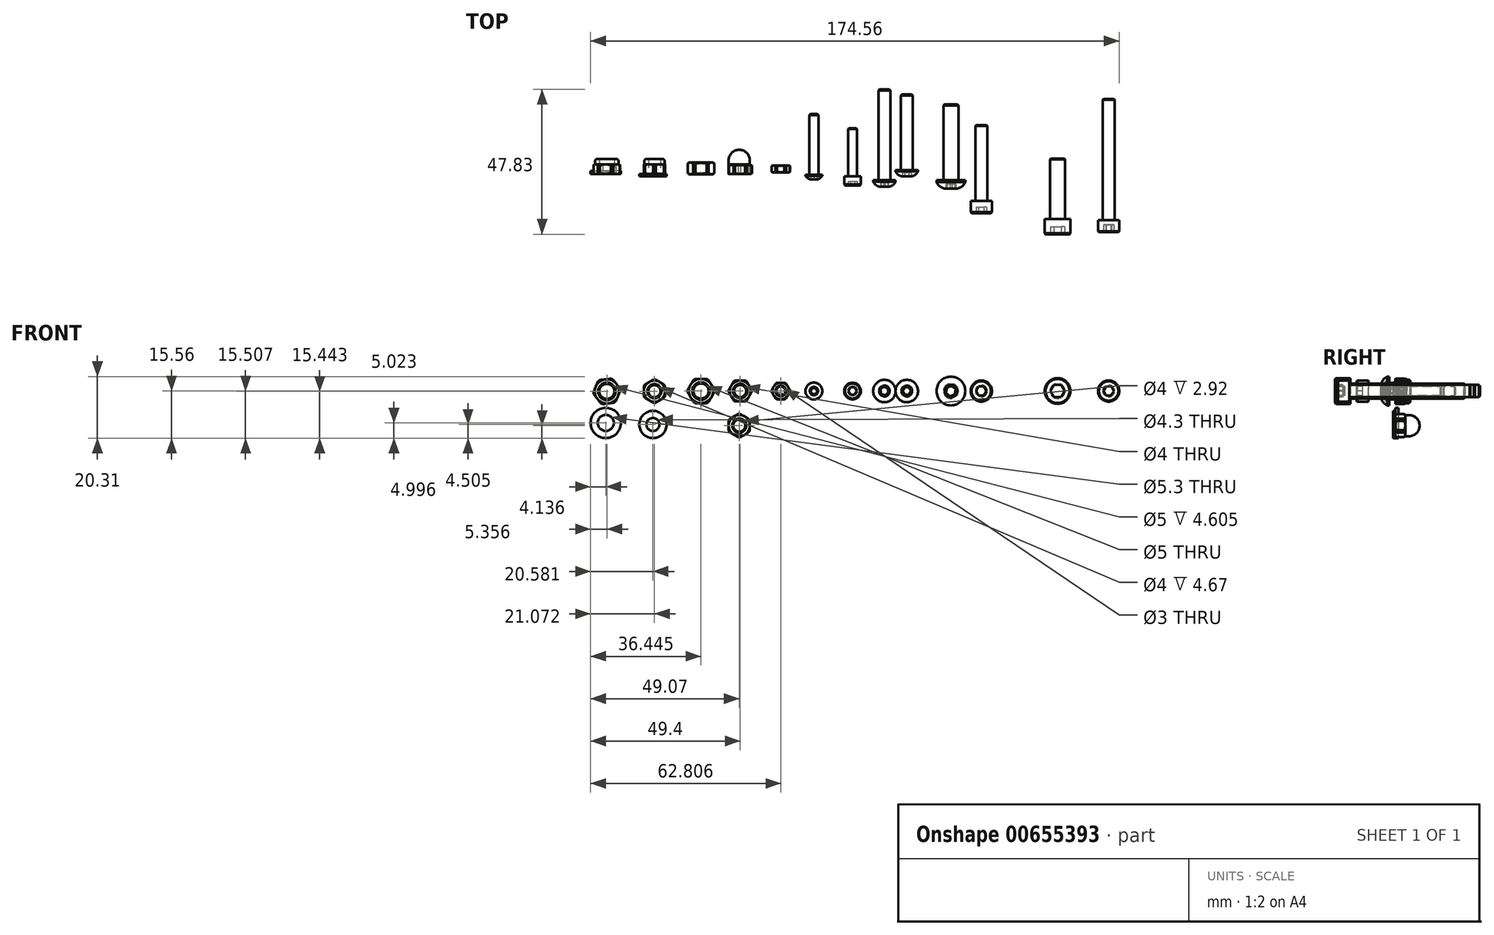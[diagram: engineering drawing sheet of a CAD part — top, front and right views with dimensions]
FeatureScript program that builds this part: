
annotation { "Feature Type Name" : "Feature", "Feature Type Description" : "" }
export const myFeature = defineFeature(function(context is Context, id is Id, definition is map)
    precondition{}
    {
        {
            var Q0;
            Q0=qCreatedBy(makeId("Top.planeOp"),FACE);
            var sketch = newSketch(context, id + "F0", { "sketchPlane" : qUnion([Q0])});
            skLineSegment(sketch, "E0.bottom", {"start": v(-2, 0) * mm, "end": v(-3.83, 0) * mm});
            skLineSegment(sketch, "E0.top", {"start": v(-2, 3) * mm, "end": v(-3.83, 3) * mm});
            skLineSegment(sketch, "E0.left", {"start": v(-2, 0) * mm, "end": v(-2, 3) * mm});
            skLineSegment(sketch, "E0.right", {"start": v(-3.83, 0) * mm, "end": v(-3.83, 3) * mm});
            skLineSegment(sketch, "E1", {"start": v(-2, 0) * mm, "end": v(0, 0) * mm, "construction": true});
            skLineSegment(sketch, "E2", {"start": v(0, 0) * mm, "end": v(0, 3) * mm, "construction": true});
            skSolve(sketch);
        }
        {
            var Q0;
            Q0 = qSketchRegion(id + "F0", true);
            var Q1;
            Q1=sQuery(id+"F0.wireOp",EDGE,"E2");
            revolve(context, id + "F1", {"entities" : qUnion([Q0]), "axis" : qUnion([Q1]), "revolveType" : RevolveType.FULL});
        }
        {
            var Q0;
            Q0=makeQuery(id+"F1.opRevolve","SWEPT_EDGE",EDGE,{"disambiguationData":[OSD([sQuery(id+"F0.wireOp",EDGE,"E0.bottom"),sQuery(id+"F0.wireOp",EDGE,"E0.right")])]});
            var Q1;
            Q1=makeQuery(id+"F1.opRevolve","SWEPT_EDGE",EDGE,{"disambiguationData":[OSD([sQuery(id+"F0.wireOp",EDGE,"E0.top"),sQuery(id+"F0.wireOp",EDGE,"E0.right")])]});
            var Q2;
            Q2=makeQuery(id+"F1.opRevolve","SWEPT_EDGE",EDGE,{"disambiguationData":[OSD([sQuery(id+"F0.wireOp",EDGE,"E0.bottom"),sQuery(id+"F0.wireOp",EDGE,"E0.left")])]});
            var Q3;
            Q3=makeQuery(id+"F1.opRevolve","SWEPT_EDGE",EDGE,{"disambiguationData":[OSD([sQuery(id+"F0.wireOp",EDGE,"E0.top"),sQuery(id+"F0.wireOp",EDGE,"E0.left")])]});
            chamfer(context, id + "F2", {"entities" : qUnion([Q0, Q1, Q2, Q3]), "chamferType" : ChamferType.OFFSET_ANGLE, "width" : 0.77 * mm / 2, "oppositeDirection" : false, "angle" : 30 * degree, "tangentPropagation" : true});
        }
        {
            var Q0;
            Q0=makeQuery(id+"F1.opRevolve","SWEPT_FACE",FACE,{"disambiguationData":[OSD([sQuery(id+"F0.wireOp",EDGE,"E0.bottom")])]});
            var sketch = newSketch(context, id + "F3", { "sketchPlane" : qUnion([Q0])});
            skCircle(sketch, "E3.cCircle", {"center": v(0, 0) * mm, "radius": 3.45 * mm, "construction": true});
            skLineSegment(sketch, "E3.0", {"start": v(3.98, 0) * mm, "end": v(2, -3.45) * mm});
            skLineSegment(sketch, "E3.1", {"start": v(2, -3.45) * mm, "end": v(-2, -3.45) * mm});
            skLineSegment(sketch, "E3.2", {"start": v(-2, -3.45) * mm, "end": v(-3.98, 0) * mm});
            skLineSegment(sketch, "E3.3", {"start": v(-3.98, 0) * mm, "end": v(-2, 3.45) * mm});
            skLineSegment(sketch, "E3.4", {"start": v(-2, 3.45) * mm, "end": v(2, 3.45) * mm});
            skLineSegment(sketch, "E3.5", {"start": v(2, 3.45) * mm, "end": v(3.98, 0) * mm});
            skPoint(sketch, "E3.0.midPoint", {"position": v(2.99, -1.73) * mm});
            skCircle(sketch, "E4", {"center": v(0, 0) * mm, "radius": 4.53 * mm});
            skSolve(sketch);
        }
        {
            var Q0;
            Q0 = qSketchRegion(id + "F3", true);
            extrude(context, id + "F4", {"entities" : qUnion([Q0]), "operationType" : NewBodyOperationType.REMOVE, "oppositeDirection" : true, "depth" : 25 * mm, "offsetDistance" : 25 * mm});
        }
        {
            var Q0;
            Q0=qCreatedBy(makeId("Top.planeOp"),FACE);
            var sketch = newSketch(context, id + "F5", { "sketchPlane" : qUnion([Q0])});
            skLineSegment(sketch, "E5.bottom", {"start": v(10.4, 2.85) * mm, "end": v(11.9, 2.85) * mm});
            skLineSegment(sketch, "E5.top", {"start": v(10.4, 0.58) * mm, "end": v(11.9, 0.58) * mm});
            skLineSegment(sketch, "E5.left", {"start": v(10.4, 2.85) * mm, "end": v(10.4, 0.58) * mm});
            skLineSegment(sketch, "E5.right", {"start": v(11.9, 2.85) * mm, "end": v(11.9, 0.58) * mm});
            skLineSegment(sketch, "E6", {"start": v(11.9, 0.58) * mm, "end": v(13.4, 0.58) * mm, "construction": true});
            skLineSegment(sketch, "E7", {"start": v(13.4, 0.58) * mm, "end": v(13.4, 2.85) * mm, "construction": true});
            skSolve(sketch);
        }
        {
            var Q0;
            Q0 = qSketchRegion(id + "F5", true);
            var Q1;
            Q1=sQuery(id+"F5.wireOp",EDGE,"E7");
            revolve(context, id + "F6", {"entities" : qUnion([Q0]), "axis" : qUnion([Q1]), "revolveType" : RevolveType.FULL});
        }
        {
            var Q0;
            Q0=makeQuery(id+"F6.opRevolve","SWEPT_EDGE",EDGE,{"disambiguationData":[OSD([sQuery(id+"F5.wireOp",EDGE,"E5.top"),sQuery(id+"F5.wireOp",EDGE,"E5.right")])]});
            var Q1;
            Q1=makeQuery(id+"F6.opRevolve","SWEPT_EDGE",EDGE,{"disambiguationData":[OSD([sQuery(id+"F5.wireOp",EDGE,"E5.top"),sQuery(id+"F5.wireOp",EDGE,"E5.left")])]});
            var Q2;
            Q2=makeQuery(id+"F6.opRevolve","SWEPT_EDGE",EDGE,{"disambiguationData":[OSD([sQuery(id+"F5.wireOp",EDGE,"E5.bottom"),sQuery(id+"F5.wireOp",EDGE,"E5.right")])]});
            var Q3;
            Q3=makeQuery(id+"F6.opRevolve","SWEPT_EDGE",EDGE,{"disambiguationData":[OSD([sQuery(id+"F5.wireOp",EDGE,"E5.bottom"),sQuery(id+"F5.wireOp",EDGE,"E5.left")])]});
            chamfer(context, id + "F7", {"entities" : qUnion([Q0, Q1, Q2, Q3]), "width" : 0.51 / 2 * mm, "tangentPropagation" : true});
        }
        {
            var Q0;
            Q0=makeQuery(id+"F6.opRevolve","SWEPT_FACE",FACE,{"disambiguationData":[OSD([sQuery(id+"F5.wireOp",EDGE,"E5.top")])]});
            var sketch = newSketch(context, id + "F8", { "sketchPlane" : qUnion([Q0])});
            skCircle(sketch, "E8.cCircle", {"center": v(13.4, 0) * mm, "radius": 2.75 * mm, "construction": true});
            skLineSegment(sketch, "E8.0", {"start": v(16.58, 0) * mm, "end": v(15, -2.75) * mm});
            skLineSegment(sketch, "E8.1", {"start": v(15, -2.75) * mm, "end": v(11.82, -2.75) * mm});
            skLineSegment(sketch, "E8.2", {"start": v(11.82, -2.75) * mm, "end": v(10.23, 0) * mm});
            skLineSegment(sketch, "E8.3", {"start": v(10.23, 0) * mm, "end": v(11.82, 2.75) * mm});
            skLineSegment(sketch, "E8.4", {"start": v(11.82, 2.75) * mm, "end": v(15, 2.75) * mm});
            skLineSegment(sketch, "E8.5", {"start": v(15, 2.75) * mm, "end": v(16.58, 0) * mm});
            skPoint(sketch, "E8.0.midPoint", {"position": v(15.79, -1.38) * mm});
            skCircle(sketch, "E9", {"center": v(13.4, 0) * mm, "radius": 3.66 * mm});
            skSolve(sketch);
        }
        {
            var Q0;
            Q0 = qSketchRegion(id + "F8", true);
            extrude(context, id + "F9", {"entities" : qUnion([Q0]), "operationType" : NewBodyOperationType.REMOVE, "oppositeDirection" : true, "depth" : 25 * mm, "offsetDistance" : 25 * mm});
        }
        {
            var Q0;
            Q0=qCreatedBy(makeId("Top.planeOp"),FACE);
            var sketch = newSketch(context, id + "F10", { "sketchPlane" : qUnion([Q0])});
            skLineSegment(sketch, "E10.bottom", {"start": v(-15.45, 3.8) * mm, "end": v(-17.35, 3.8) * mm});
            skLineSegment(sketch, "E10.top", {"start": v(-15.45, -0.05) * mm, "end": v(-17.35, -0.05) * mm});
            skLineSegment(sketch, "E10.left", {"start": v(-15.45, 3.8) * mm, "end": v(-15.45, -0.05) * mm});
            skLineSegment(sketch, "E10.right", {"start": v(-17.35, 3.8) * mm, "end": v(-17.35, -0.05) * mm});
            skLineSegment(sketch, "E11", {"start": v(-15.45, 3.8) * mm, "end": v(-12.95, 3.8) * mm, "construction": true});
            skLineSegment(sketch, "E12", {"start": v(-12.95, 3.8) * mm, "end": v(-12.95, -0.05) * mm, "construction": true});
            skSolve(sketch);
        }
        {
            var Q0;
            Q0 = qSketchRegion(id + "F10", true);
            var Q1;
            Q1=sQuery(id+"F10.wireOp",EDGE,"E12");
            revolve(context, id + "F11", {"entities" : qUnion([Q0]), "axis" : qUnion([Q1]), "revolveType" : RevolveType.FULL});
        }
        {
            var Q0;
            Q0=makeQuery(id+"F11.opRevolve","SWEPT_EDGE",EDGE,{"disambiguationData":[OSD([sQuery(id+"F10.wireOp",EDGE,"E10.bottom"),sQuery(id+"F10.wireOp",EDGE,"E10.left")])]});
            var Q1;
            Q1=makeQuery(id+"F11.opRevolve","SWEPT_EDGE",EDGE,{"disambiguationData":[OSD([sQuery(id+"F10.wireOp",EDGE,"E10.bottom"),sQuery(id+"F10.wireOp",EDGE,"E10.right")])]});
            var Q2;
            Q2=makeQuery(id+"F11.opRevolve","SWEPT_EDGE",EDGE,{"disambiguationData":[OSD([sQuery(id+"F10.wireOp",EDGE,"E10.top"),sQuery(id+"F10.wireOp",EDGE,"E10.left")])]});
            var Q3;
            Q3=makeQuery(id+"F11.opRevolve","SWEPT_EDGE",EDGE,{"disambiguationData":[OSD([sQuery(id+"F10.wireOp",EDGE,"E10.top"),sQuery(id+"F10.wireOp",EDGE,"E10.right")])]});
            chamfer(context, id + "F12", {"entities" : qUnion([Q0, Q1, Q2, Q3]), "width" : 0.4 * mm, "tangentPropagation" : true});
        }
        {
            var Q0;
            Q0=makeQuery(id+"F11.opRevolve","SWEPT_FACE",FACE,{"disambiguationData":[OSD([sQuery(id+"F10.wireOp",EDGE,"E10.top")])]});
            var sketch = newSketch(context, id + "F13", { "sketchPlane" : qUnion([Q0])});
            skCircle(sketch, "E13.cCircle", {"center": v(-12.95, 0) * mm, "radius": 4 * mm, "construction": true});
            skLineSegment(sketch, "E13.0", {"start": v(-8.34, 0) * mm, "end": v(-10.65, -4) * mm});
            skLineSegment(sketch, "E13.1", {"start": v(-10.65, -4) * mm, "end": v(-15.26, -4) * mm});
            skLineSegment(sketch, "E13.2", {"start": v(-15.26, -4) * mm, "end": v(-17.57, 0) * mm});
            skLineSegment(sketch, "E13.3", {"start": v(-17.57, 0) * mm, "end": v(-15.26, 4) * mm});
            skLineSegment(sketch, "E13.4", {"start": v(-15.26, 4) * mm, "end": v(-10.65, 4) * mm});
            skLineSegment(sketch, "E13.5", {"start": v(-10.65, 4) * mm, "end": v(-8.34, 0) * mm});
            skPoint(sketch, "E13.0.midPoint", {"position": v(-9.5, -2) * mm});
            skCircle(sketch, "E14", {"center": v(-12.95, 0) * mm, "radius": 5.32 * mm});
            skSolve(sketch);
        }
        {
            var Q0;
            Q0 = qSketchRegion(id + "F13", true);
            extrude(context, id + "F14", {"entities" : qUnion([Q0]), "operationType" : NewBodyOperationType.REMOVE, "oppositeDirection" : true, "depth" : 25 * mm, "offsetDistance" : 25 * mm});
        }
        {
            var Q0;
            Q0=qCreatedBy(makeId("Top.planeOp"),FACE);
            var sketch = newSketch(context, id + "F15", { "sketchPlane" : qUnion([Q0])});
            skLineSegment(sketch, "E15", {"start": v(24.32, 19.82) * mm, "end": v(24.32, -1.7) * mm});
            skLineSegment(sketch, "E16", {"start": v(24.32, -1.7) * mm, "end": v(22.95, -1.7) * mm});
            skLineSegment(sketch, "E17", {"start": v(21.55, -0.58) * mm, "end": v(21.55, -0.18) * mm});
            skLineSegment(sketch, "E18", {"start": v(21.55, -0.18) * mm, "end": v(22.82, -0.18) * mm});
            skLineSegment(sketch, "E19", {"start": v(22.82, -0.18) * mm, "end": v(22.82, 19.41) * mm});
            skLineSegment(sketch, "E20", {"start": v(22.82, 19.41) * mm, "end": v(23.18, 19.82) * mm});
            skLineSegment(sketch, "E21", {"start": v(23.18, 19.82) * mm, "end": v(24.32, 19.82) * mm});
            skArc(sketch, "E22", {"start": v(22.95, -1.7) * mm, "mid": v(22.16, -1.26) * mm, "end": v(21.55, -0.58) * mm});
            skSolve(sketch);
        }
        {
            var Q0;
            Q0 = qSketchRegion(id + "F15", true);
            var Q1;
            Q1=sQuery(id+"F15.wireOp",EDGE,"E15");
            revolve(context, id + "F16", {"entities" : qUnion([Q0]), "axis" : qUnion([Q1]), "revolveType" : RevolveType.FULL});
        }
        {
            var Q0;
            Q0=makeQuery(id+"F16.opRevolve","SWEPT_FACE",FACE,{"disambiguationData":[OSD([sQuery(id+"F15.wireOp",EDGE,"E16")])]});
            var sketch = newSketch(context, id + "F17", { "sketchPlane" : qUnion([Q0])});
            skCircle(sketch, "E23.cCircle", {"center": v(24.32, 0) * mm, "radius": 1.02 * mm, "construction": true});
            skLineSegment(sketch, "E23.0", {"start": v(25.34, 0.59) * mm, "end": v(25.34, -0.59) * mm});
            skLineSegment(sketch, "E23.1", {"start": v(25.34, -0.59) * mm, "end": v(24.32, -1.17) * mm});
            skLineSegment(sketch, "E23.2", {"start": v(24.32, -1.17) * mm, "end": v(23.3, -0.59) * mm});
            skLineSegment(sketch, "E23.3", {"start": v(23.3, -0.59) * mm, "end": v(23.3, 0.59) * mm});
            skLineSegment(sketch, "E23.4", {"start": v(23.3, 0.59) * mm, "end": v(24.32, 1.17) * mm});
            skLineSegment(sketch, "E23.5", {"start": v(24.32, 1.17) * mm, "end": v(25.34, 0.59) * mm});
            skPoint(sketch, "E23.0.midPoint", {"position": v(25.34, 0) * mm});
            skSolve(sketch);
        }
        {
            var Q0;
            Q0 = qSketchRegion(id + "F17", true);
            extrude(context, id + "F18", {"entities" : qUnion([Q0]), "operationType" : NewBodyOperationType.REMOVE, "oppositeDirection" : true, "depth" : 1.04 * mm, "offsetDistance" : 25 * mm});
        }
        {
            var Q0;
            Q0=qCreatedBy(makeId("Top.planeOp"),FACE);
            var sketch = newSketch(context, id + "F19", { "sketchPlane" : qUnion([Q0])});
            skLineSegment(sketch, "E24.bottom", {"start": v(34.33, -0.72) * mm, "end": v(35.58, -0.72) * mm});
            skLineSegment(sketch, "E24.top", {"start": v(34.61, -3.72) * mm, "end": v(37.08, -3.72) * mm});
            skLineSegment(sketch, "E24.left", {"start": v(34.33, -0.72) * mm, "end": v(34.33, -3.44) * mm});
            skLineSegment(sketch, "E24.right", {"start": v(37.08, -0.72) * mm, "end": v(37.08, -3.72) * mm});
            skLineSegment(sketch, "E25.top", {"start": v(37.08, 15.2) * mm, "end": v(35.86, 15.2) * mm});
            skLineSegment(sketch, "E25.left", {"start": v(37.08, -0.72) * mm, "end": v(37.08, 15.2) * mm});
            skLineSegment(sketch, "E25.right", {"start": v(35.58, -0.72) * mm, "end": v(35.58, 14.92) * mm});
            skLineSegment(sketch, "E26", {"start": v(34.33, -3.44) * mm, "end": v(34.61, -3.72) * mm});
            skLineSegment(sketch, "E27", {"start": v(35.58, 14.92) * mm, "end": v(35.86, 15.2) * mm});
            skSolve(sketch);
        }
        {
            var Q0;
            Q0 = qSketchRegion(id + "F19", true);
            var Q1;
            Q1=sQuery(id+"F19.wireOp",EDGE,"E25.left");
            revolve(context, id + "F20", {"entities" : qUnion([Q0]), "axis" : qUnion([Q1]), "revolveType" : RevolveType.FULL});
        }
        {
            var Q0;
            Q0=makeQuery(id+"F20.opRevolve","SWEPT_FACE",FACE,{"disambiguationData":[OSD([sQuery(id+"F19.wireOp",EDGE,"E24.top")])]});
            var sketch = newSketch(context, id + "F21", { "sketchPlane" : qUnion([Q0])});
            skCircle(sketch, "E28.cCircle", {"center": v(37.08, 0) * mm, "radius": 1.25 * mm, "construction": true});
            skLineSegment(sketch, "E28.0", {"start": v(37.8, 1.25) * mm, "end": v(38.52, 0) * mm});
            skLineSegment(sketch, "E28.1", {"start": v(38.52, 0) * mm, "end": v(37.8, -1.25) * mm});
            skLineSegment(sketch, "E28.2", {"start": v(37.8, -1.25) * mm, "end": v(36.36, -1.25) * mm});
            skLineSegment(sketch, "E28.3", {"start": v(36.36, -1.25) * mm, "end": v(35.64, 0) * mm});
            skLineSegment(sketch, "E28.4", {"start": v(35.64, 0) * mm, "end": v(36.36, 1.25) * mm});
            skLineSegment(sketch, "E28.5", {"start": v(36.36, 1.25) * mm, "end": v(37.8, 1.25) * mm});
            skPoint(sketch, "E28.0.midPoint", {"position": v(38.16, 0.62) * mm});
            skSolve(sketch);
        }
        {
            var Q0;
            Q0 = qSketchRegion(id + "F21", true);
            extrude(context, id + "F22", {"entities" : qUnion([Q0]), "operationType" : NewBodyOperationType.REMOVE, "oppositeDirection" : true, "depth" : 1.3 * mm, "offsetDistance" : 25 * mm});
        }
        {
            var Q0;
            Q0=qCreatedBy(makeId("Top.planeOp"),FACE);
            var sketch = newSketch(context, id + "F23", { "sketchPlane" : qUnion([Q0])});
            skLineSegment(sketch, "E29", {"start": v(55, 26.35) * mm, "end": v(55, -0.73) * mm});
            skLineSegment(sketch, "E30", {"start": v(55, -0.73) * mm, "end": v(53.25, -0.73) * mm});
            skLineSegment(sketch, "E31", {"start": v(51.3, 0.95) * mm, "end": v(51.3, 1.35) * mm});
            skLineSegment(sketch, "E32", {"start": v(51.3, 1.35) * mm, "end": v(53, 1.35) * mm});
            skLineSegment(sketch, "E33", {"start": v(53, 1.35) * mm, "end": v(53, 25.94) * mm});
            skLineSegment(sketch, "E34", {"start": v(53, 25.94) * mm, "end": v(53.36, 26.35) * mm});
            skLineSegment(sketch, "E35", {"start": v(53.36, 26.35) * mm, "end": v(55, 26.35) * mm});
            skArc(sketch, "E36", {"start": v(53.25, -0.73) * mm, "mid": v(52.07, -0.12) * mm, "end": v(51.3, 0.95) * mm});
            skSolve(sketch);
        }
        {
            var Q0;
            Q0 = qSketchRegion(id + "F23", true);
            var Q1;
            Q1=sQuery(id+"F23.wireOp",EDGE,"E29");
            revolve(context, id + "F24", {"entities" : qUnion([Q0]), "axis" : qUnion([Q1]), "revolveType" : RevolveType.FULL});
        }
        {
            var Q0;
            Q0=makeQuery(id+"F24.opRevolve","SWEPT_FACE",FACE,{"disambiguationData":[OSD([sQuery(id+"F23.wireOp",EDGE,"E30")])]});
            var sketch = newSketch(context, id + "F25", { "sketchPlane" : qUnion([Q0])});
            skCircle(sketch, "E37.cCircle", {"center": v(55, 0) * mm, "radius": 1.27 * mm, "construction": true});
            skLineSegment(sketch, "E37.0", {"start": v(56.47, 0) * mm, "end": v(55.73, -1.27) * mm});
            skLineSegment(sketch, "E37.1", {"start": v(55.73, -1.27) * mm, "end": v(54.27, -1.27) * mm});
            skLineSegment(sketch, "E37.2", {"start": v(54.27, -1.27) * mm, "end": v(53.53, 0) * mm});
            skLineSegment(sketch, "E37.3", {"start": v(53.53, 0) * mm, "end": v(54.27, 1.27) * mm});
            skLineSegment(sketch, "E37.4", {"start": v(54.27, 1.27) * mm, "end": v(55.73, 1.27) * mm});
            skLineSegment(sketch, "E37.5", {"start": v(55.73, 1.27) * mm, "end": v(56.47, 0) * mm});
            skPoint(sketch, "E37.0.midPoint", {"position": v(56.1, -0.64) * mm});
            skSolve(sketch);
        }
        {
            var Q0;
            Q0 = qSketchRegion(id + "F25", true);
            extrude(context, id + "F26", {"entities" : qUnion([Q0]), "operationType" : NewBodyOperationType.REMOVE, "oppositeDirection" : true, "depth" : 1.3 * mm, "offsetDistance" : 25 * mm});
        }
        {
            var Q0;
            Q0=qCreatedBy(makeId("Top.planeOp"),FACE);
            var sketch = newSketch(context, id + "F27", { "sketchPlane" : qUnion([Q0])});
            skLineSegment(sketch, "E38.bottom", {"start": v(76.11, -8.88) * mm, "end": v(77.61, -8.88) * mm});
            skLineSegment(sketch, "E38.top", {"start": v(76.4, -12.88) * mm, "end": v(79.61, -12.88) * mm});
            skLineSegment(sketch, "E38.left", {"start": v(76.11, -8.88) * mm, "end": v(76.11, -12.6) * mm});
            skLineSegment(sketch, "E38.right", {"start": v(79.61, -8.88) * mm, "end": v(79.61, -12.88) * mm});
            skLineSegment(sketch, "E39.top", {"start": v(79.61, 16.12) * mm, "end": v(77.9, 16.12) * mm});
            skLineSegment(sketch, "E39.left", {"start": v(79.61, -8.88) * mm, "end": v(79.61, 16.12) * mm});
            skLineSegment(sketch, "E39.right", {"start": v(77.61, -8.88) * mm, "end": v(77.61, 15.84) * mm});
            skLineSegment(sketch, "E40", {"start": v(76.11, -12.6) * mm, "end": v(76.4, -12.88) * mm});
            skLineSegment(sketch, "E41", {"start": v(77.61, 15.84) * mm, "end": v(77.9, 16.12) * mm});
            skSolve(sketch);
        }
        {
            var Q0;
            Q0 = qSketchRegion(id + "F27", true);
            var Q1;
            Q1=sQuery(id+"F27.wireOp",EDGE,"E39.left");
            revolve(context, id + "F28", {"entities" : qUnion([Q0]), "axis" : qUnion([Q1]), "revolveType" : RevolveType.FULL});
        }
        {
            var Q0;
            Q0=makeQuery(id+"F28.opRevolve","SWEPT_FACE",FACE,{"disambiguationData":[OSD([sQuery(id+"F27.wireOp",EDGE,"E38.top")])]});
            var sketch = newSketch(context, id + "F29", { "sketchPlane" : qUnion([Q0])});
            skCircle(sketch, "E42.cCircle", {"center": v(79.61, 0) * mm, "radius": 1.5 * mm, "construction": true});
            skLineSegment(sketch, "E42.0", {"start": v(81.34, 0) * mm, "end": v(80.48, -1.5) * mm});
            skLineSegment(sketch, "E42.1", {"start": v(80.48, -1.5) * mm, "end": v(78.75, -1.5) * mm});
            skLineSegment(sketch, "E42.2", {"start": v(78.75, -1.5) * mm, "end": v(77.88, 0) * mm});
            skLineSegment(sketch, "E42.3", {"start": v(77.88, 0) * mm, "end": v(78.75, 1.5) * mm});
            skLineSegment(sketch, "E42.4", {"start": v(78.75, 1.5) * mm, "end": v(80.48, 1.5) * mm});
            skLineSegment(sketch, "E42.5", {"start": v(80.48, 1.5) * mm, "end": v(81.34, 0) * mm});
            skPoint(sketch, "E42.0.midPoint", {"position": v(80.91, -0.75) * mm});
            skSolve(sketch);
        }
        {
            var Q0;
            Q0 = qSketchRegion(id + "F29", true);
            extrude(context, id + "F30", {"entities" : qUnion([Q0]), "operationType" : NewBodyOperationType.REMOVE, "oppositeDirection" : true, "depth" : 2 * mm, "offsetDistance" : 25 * mm});
        }
        {
            var Q0;
            Q0=qCreatedBy(makeId("Top.planeOp"),FACE);
            var sketch = newSketch(context, id + "F31", { "sketchPlane" : qUnion([Q0])});
            skLineSegment(sketch, "E43.bottom", {"start": v(100.55, -14.88) * mm, "end": v(102.3, -14.88) * mm});
            skLineSegment(sketch, "E43.top", {"start": v(100.83, -19.88) * mm, "end": v(104.8, -19.88) * mm});
            skLineSegment(sketch, "E43.left", {"start": v(100.55, -14.88) * mm, "end": v(100.55, -19.6) * mm});
            skLineSegment(sketch, "E43.right", {"start": v(104.8, -14.88) * mm, "end": v(104.8, -19.88) * mm});
            skLineSegment(sketch, "E44.top", {"start": v(104.8, 5.12) * mm, "end": v(102.58, 5.12) * mm});
            skLineSegment(sketch, "E44.left", {"start": v(104.8, -14.88) * mm, "end": v(104.8, 5.12) * mm});
            skLineSegment(sketch, "E44.right", {"start": v(102.3, -14.88) * mm, "end": v(102.3, 4.84) * mm});
            skLineSegment(sketch, "E45", {"start": v(100.55, -19.6) * mm, "end": v(100.83, -19.88) * mm});
            skLineSegment(sketch, "E46", {"start": v(102.3, 4.84) * mm, "end": v(102.58, 5.12) * mm});
            skSolve(sketch);
        }
        {
            var Q0;
            Q0 = qSketchRegion(id + "F31", true);
            var Q1;
            Q1=sQuery(id+"F31.wireOp",EDGE,"E43.right");
            revolve(context, id + "F32", {"entities" : qUnion([Q0]), "axis" : qUnion([Q1]), "revolveType" : RevolveType.FULL});
        }
        {
            var Q0;
            Q0=makeQuery(id+"F32.opRevolve","SWEPT_FACE",FACE,{"disambiguationData":[OSD([sQuery(id+"F31.wireOp",EDGE,"E43.top")])]});
            var sketch = newSketch(context, id + "F33", { "sketchPlane" : qUnion([Q0])});
            skCircle(sketch, "E47.cCircle", {"center": v(104.8, 0) * mm, "radius": 2 * mm, "construction": true});
            skLineSegment(sketch, "E47.0", {"start": v(107.1, 0) * mm, "end": v(105.95, -2) * mm});
            skLineSegment(sketch, "E47.1", {"start": v(105.95, -2) * mm, "end": v(103.64, -2) * mm});
            skLineSegment(sketch, "E47.2", {"start": v(103.64, -2) * mm, "end": v(102.49, 0) * mm});
            skLineSegment(sketch, "E47.3", {"start": v(102.49, 0) * mm, "end": v(103.64, 2) * mm});
            skLineSegment(sketch, "E47.4", {"start": v(103.64, 2) * mm, "end": v(105.95, 2) * mm});
            skLineSegment(sketch, "E47.5", {"start": v(105.95, 2) * mm, "end": v(107.1, 0) * mm});
            skPoint(sketch, "E47.0.midPoint", {"position": v(106.53, -1) * mm});
            skSolve(sketch);
        }
        {
            var Q0;
            Q0 = qSketchRegion(id + "F33", true);
            extrude(context, id + "F34", {"entities" : qUnion([Q0]), "operationType" : NewBodyOperationType.REMOVE, "oppositeDirection" : true, "depth" : 2.5 * mm, "offsetDistance" : 25 * mm});
        }
        {
            var Q0;
            Q0=qCreatedBy(makeId("Top.planeOp"),FACE);
            var sketch = newSketch(context, id + "F35", { "sketchPlane" : qUnion([Q0])});
            skLineSegment(sketch, "E48.bottom", {"start": v(118.16, -15.2) * mm, "end": v(119.66, -15.2) * mm});
            skLineSegment(sketch, "E48.top", {"start": v(118.45, -19.2) * mm, "end": v(121.66, -19.2) * mm});
            skLineSegment(sketch, "E48.left", {"start": v(118.16, -15.2) * mm, "end": v(118.16, -18.93) * mm});
            skLineSegment(sketch, "E48.right", {"start": v(121.66, -15.2) * mm, "end": v(121.66, -19.2) * mm});
            skLineSegment(sketch, "E49.top", {"start": v(121.66, 24.8) * mm, "end": v(119.95, 24.8) * mm});
            skLineSegment(sketch, "E49.left", {"start": v(121.66, -15.2) * mm, "end": v(121.66, 24.8) * mm});
            skLineSegment(sketch, "E49.right", {"start": v(119.66, -15.2) * mm, "end": v(119.66, 24.5) * mm});
            skLineSegment(sketch, "E50", {"start": v(118.16, -18.93) * mm, "end": v(118.45, -19.2) * mm});
            skLineSegment(sketch, "E51", {"start": v(119.66, 24.5) * mm, "end": v(119.95, 24.8) * mm});
            skSolve(sketch);
        }
        {
            var Q0;
            Q0 = qSketchRegion(id + "F35", true);
            var Q1;
            Q1=sQuery(id+"F35.wireOp",EDGE,"E49.left");
            revolve(context, id + "F36", {"entities" : qUnion([Q0]), "axis" : qUnion([Q1]), "revolveType" : RevolveType.FULL});
        }
        {
            var Q0;
            Q0=makeQuery(id+"F36.opRevolve","SWEPT_FACE",FACE,{"disambiguationData":[OSD([sQuery(id+"F35.wireOp",EDGE,"E48.top")])]});
            var sketch = newSketch(context, id + "F37", { "sketchPlane" : qUnion([Q0])});
            skCircle(sketch, "E52.cCircle", {"center": v(121.66, 0) * mm, "radius": 1.5 * mm, "construction": true});
            skLineSegment(sketch, "E52.0", {"start": v(122.62, 1.44) * mm, "end": v(123.4, -0.1) * mm});
            skLineSegment(sketch, "E52.1", {"start": v(123.4, -0.1) * mm, "end": v(122.43, -1.55) * mm});
            skLineSegment(sketch, "E52.2", {"start": v(122.43, -1.55) * mm, "end": v(120.7, -1.44) * mm});
            skLineSegment(sketch, "E52.3", {"start": v(120.7, -1.44) * mm, "end": v(119.94, 0.1) * mm});
            skLineSegment(sketch, "E52.4", {"start": v(119.94, 0.1) * mm, "end": v(120.9, 1.55) * mm});
            skLineSegment(sketch, "E52.5", {"start": v(120.9, 1.55) * mm, "end": v(122.62, 1.44) * mm});
            skPoint(sketch, "E52.0.midPoint", {"position": v(123, 0.67) * mm});
            skSolve(sketch);
        }
        {
            var Q0;
            Q0 = qSketchRegion(id + "F37", true);
            extrude(context, id + "F38", {"entities" : qUnion([Q0]), "operationType" : NewBodyOperationType.REMOVE, "oppositeDirection" : true, "depth" : 2.5 * mm, "offsetDistance" : 25 * mm});
        }
        {
            var Q0;
            Q0=qCreatedBy(makeId("Front.planeOp"),FACE);
            var sketch = newSketch(context, id + "F39", { "sketchPlane" : qUnion([Q0])});
            skCircle(sketch, "E53", {"center": v(-28.33, -0.05) * mm, "radius": 3.83 * mm});
            skCircle(sketch, "E54", {"center": v(-28.33, -0.05) * mm, "radius": 2 * mm});
            skSolve(sketch);
        }
        {
            var Q0;
            Q0 = qSketchRegion(id + "F39", true);
            extrude(context, id + "F40", {"entities" : qUnion([Q0]), "oppositeDirection" : true, "depth" : 3.25 * mm, "offsetDistance" : 25 * mm});
        }
        {
            var Q0;
            Q0=makeQuery(id+"F40.opExtrude","CAP_EDGE",EDGE,{"disambiguationData":[OSD([sQuery(id+"F39.wireOp",EDGE,"E53")])],"isStart":false});
            var Q1;
            Q1=makeQuery(id+"F40.opExtrude","CAP_EDGE",EDGE,{"disambiguationData":[OSD([sQuery(id+"F39.wireOp",EDGE,"E53")])],"isStart":true});
            var Q2;
            Q2=makeQuery(id+"F40.opExtrude","CAP_EDGE",EDGE,{"disambiguationData":[OSD([sQuery(id+"F39.wireOp",EDGE,"E54")])],"isStart":true});
            chamfer(context, id + "F41", {"entities" : qUnion([Q0, Q1, Q2]), "width" : 0.66 / 2 * mm, "tangentPropagation" : true});
        }
        {
            var Q0;
            Q0=makeQuery(id+"F40.opExtrude","CAP_FACE",FACE,{"disambiguationData":[OSD([sQuery(id+"F39.wireOp",EDGE,"E53"),sQuery(id+"F39.wireOp",EDGE,"E54")])],"isStart":false});
            var sketch = newSketch(context, id + "F42", { "sketchPlane" : qUnion([Q0])});
            skCircle(sketch, "E55.cCircle", {"center": v(28.33, -0.05) * mm, "radius": 3.5 * mm, "construction": true});
            skLineSegment(sketch, "E55.0", {"start": v(31.83, 1.97) * mm, "end": v(31.83, -2.07) * mm});
            skLineSegment(sketch, "E55.1", {"start": v(31.83, -2.07) * mm, "end": v(28.33, -4.1) * mm});
            skLineSegment(sketch, "E55.2", {"start": v(28.33, -4.1) * mm, "end": v(24.83, -2.07) * mm});
            skLineSegment(sketch, "E55.3", {"start": v(24.83, -2.07) * mm, "end": v(24.83, 1.97) * mm});
            skLineSegment(sketch, "E55.4", {"start": v(24.83, 1.97) * mm, "end": v(28.33, 3.99) * mm});
            skLineSegment(sketch, "E55.5", {"start": v(28.33, 3.99) * mm, "end": v(31.83, 1.97) * mm});
            skPoint(sketch, "E55.0.midPoint", {"position": v(31.83, -0.05) * mm});
            skCircle(sketch, "E56", {"center": v(28.33, -0.05) * mm, "radius": 6.48 * mm});
            skSolve(sketch);
        }
        {
            var Q0;
            Q0 = qSketchRegion(id + "F42", true);
            extrude(context, id + "F43", {"entities" : qUnion([Q0]), "operationType" : NewBodyOperationType.REMOVE, "oppositeDirection" : true, "depth" : 25 * mm, "offsetDistance" : 25 * mm});
        }
        {
            var Q0;
            Q0=makeQuery(id+"F40.opExtrude","CAP_FACE",FACE,{"disambiguationData":[OSD([sQuery(id+"F39.wireOp",EDGE,"E53"),sQuery(id+"F39.wireOp",EDGE,"E54")])],"isStart":false});
            var sketch = newSketch(context, id + "F44", { "sketchPlane" : qUnion([Q0])});
            skCircle(sketch, "E57", {"center": v(28.33, -0.05) * mm, "radius": 2 * mm});
            skCircle(sketch, "E58", {"center": v(28.33, -0.05) * mm, "radius": 3.38 * mm});
            skSolve(sketch);
        }
        {
            var Q0;
            Q0 = qSketchRegion(id + "F44", true);
            extrude(context, id + "F45", {"entities" : qUnion([Q0]), "operationType" : NewBodyOperationType.ADD, "depth" : (5 - 3.25) * mm, "offsetDistance" : 25 * mm});
        }
        {
            var Q0;
            Q0=makeQuery(id+"F45.opExtrude","CAP_EDGE",EDGE,{"disambiguationData":[OSD([sQuery(id+"F44.wireOp",EDGE,"E58")])],"isStart":false});
            fillet(context, id + "F46", {"entities" : qUnion([Q0]), "radius" : 0.75 * mm, "tangentPropagation" : true, "allowEdgeOverflow" : false});
        }
        {
            var Q0;
            Q0=qCreatedBy(makeId("Top.planeOp"),FACE);
            var sketch = newSketch(context, id + "F47", { "sketchPlane" : qUnion([Q0])});
            skLineSegment(sketch, "E59", {"start": v(69.58, 22.98) * mm, "end": v(69.58, -4.77) * mm});
            skLineSegment(sketch, "E60", {"start": v(69.58, -4.77) * mm, "end": v(67.48, -4.77) * mm});
            skLineSegment(sketch, "E61", {"start": v(64.83, -2.62) * mm, "end": v(64.83, -2.02) * mm});
            skLineSegment(sketch, "E62", {"start": v(64.83, -2.02) * mm, "end": v(67.08, -2.02) * mm});
            skLineSegment(sketch, "E63", {"start": v(67.08, -2.02) * mm, "end": v(67.08, 22.58) * mm});
            skLineSegment(sketch, "E64", {"start": v(67.08, 22.58) * mm, "end": v(67.44, 22.98) * mm});
            skLineSegment(sketch, "E65", {"start": v(67.44, 22.98) * mm, "end": v(69.58, 22.98) * mm});
            skArc(sketch, "E66", {"start": v(67.48, -4.77) * mm, "mid": v(65.88, -4.03) * mm, "end": v(64.83, -2.62) * mm});
            skSolve(sketch);
        }
        {
            var Q0;
            Q0=makeQuery(id+"F47.imprint","IMPRINT",FACE,{"disambiguationData":[TD([[makeQuery(id+"F47.imprint","IMPRINT",EDGE,{"derivedFrom":sQuery(id+"F47.wireOp",EDGE,"E59")}),-1.0]])]});
            var Q1;
            Q1=sQuery(id+"F47.wireOp",EDGE,"E59");
            revolve(context, id + "F48", {"entities" : qUnion([Q0]), "axis" : qUnion([Q1]), "revolveType" : RevolveType.FULL});
        }
        {
            var Q0;
            Q0=makeQuery(id+"F48.opRevolve","SWEPT_FACE",FACE,{"disambiguationData":[OSD([sQuery(id+"F47.wireOp",EDGE,"E60")])]});
            var sketch = newSketch(context, id + "F49", { "sketchPlane" : qUnion([Q0])});
            skCircle(sketch, "E67.cCircle", {"center": v(69.58, 0) * mm, "radius": 1.5 * mm, "construction": true});
            skLineSegment(sketch, "E67.0", {"start": v(69.92, 1.7) * mm, "end": v(71.22, 0.55) * mm});
            skLineSegment(sketch, "E67.1", {"start": v(71.22, 0.55) * mm, "end": v(70.88, -1.14) * mm});
            skLineSegment(sketch, "E67.2", {"start": v(70.88, -1.14) * mm, "end": v(69.24, -1.7) * mm});
            skLineSegment(sketch, "E67.3", {"start": v(69.24, -1.7) * mm, "end": v(67.94, -0.55) * mm});
            skLineSegment(sketch, "E67.4", {"start": v(67.94, -0.55) * mm, "end": v(68.28, 1.14) * mm});
            skLineSegment(sketch, "E67.5", {"start": v(68.28, 1.14) * mm, "end": v(69.92, 1.7) * mm});
            skPoint(sketch, "E67.0.midPoint", {"position": v(70.57, 1.13) * mm});
            skSolve(sketch);
        }
        {
            var Q0;
            Q0 = qSketchRegion(id + "F49", true);
            extrude(context, id + "F50", {"entities" : qUnion([Q0]), "operationType" : NewBodyOperationType.REMOVE, "oppositeDirection" : true, "depth" : 1.56 * mm, "offsetDistance" : 25 * mm});
        }
        {
            var Q0;
            Q0=qCreatedBy(makeId("Front.planeOp"),FACE);
            var sketch = newSketch(context, id + "F51", { "sketchPlane" : qUnion([Q0])});
            skCircle(sketch, "E68", {"center": v(-44.04, -0.12) * mm, "radius": 4.4 * mm});
            skCircle(sketch, "E69", {"center": v(-44.04, -0.12) * mm, "radius": 2.5 * mm});
            skSolve(sketch);
        }
        {
            var Q0;
            Q0 = qSketchRegion(id + "F51", true);
            extrude(context, id + "F52", {"entities" : qUnion([Q0]), "oppositeDirection" : true, "depth" : 3.25 * mm, "offsetDistance" : 25 * mm});
        }
        {
            var Q0;
            Q0=makeQuery(id+"F52.opExtrude","CAP_EDGE",EDGE,{"disambiguationData":[OSD([sQuery(id+"F51.wireOp",EDGE,"E68")])],"isStart":false});
            var Q1;
            Q1=makeQuery(id+"F52.opExtrude","CAP_EDGE",EDGE,{"disambiguationData":[OSD([sQuery(id+"F51.wireOp",EDGE,"E68")])],"isStart":true});
            var Q2;
            Q2=makeQuery(id+"F52.opExtrude","CAP_EDGE",EDGE,{"disambiguationData":[OSD([sQuery(id+"F51.wireOp",EDGE,"E69")])],"isStart":true});
            chamfer(context, id + "F53", {"entities" : qUnion([Q0, Q1, Q2]), "width" : (0.79 / 2) * mm, "tangentPropagation" : true});
        }
        {
            var Q0;
            Q0=makeQuery(id+"F52.opExtrude","CAP_FACE",FACE,{"disambiguationData":[OSD([sQuery(id+"F51.wireOp",EDGE,"E68"),sQuery(id+"F51.wireOp",EDGE,"E69")])],"isStart":false});
            var sketch = newSketch(context, id + "F54", { "sketchPlane" : qUnion([Q0])});
            skCircle(sketch, "E70.cCircle", {"center": v(44.04, -0.12) * mm, "radius": 4 * mm, "construction": true});
            skLineSegment(sketch, "E70.0", {"start": v(39.46, 0.47) * mm, "end": v(42.26, 4.14) * mm});
            skLineSegment(sketch, "E70.1", {"start": v(42.26, 4.14) * mm, "end": v(46.84, 3.56) * mm});
            skLineSegment(sketch, "E70.2", {"start": v(46.84, 3.56) * mm, "end": v(48.63, -0.7) * mm});
            skLineSegment(sketch, "E70.3", {"start": v(48.63, -0.7) * mm, "end": v(45.83, -4.38) * mm});
            skLineSegment(sketch, "E70.4", {"start": v(45.83, -4.38) * mm, "end": v(41.25, -3.8) * mm});
            skLineSegment(sketch, "E70.5", {"start": v(41.25, -3.8) * mm, "end": v(39.46, 0.47) * mm});
            skPoint(sketch, "E70.0.midPoint", {"position": v(40.86, 2.3) * mm});
            skCircle(sketch, "E71", {"center": v(44.04, -0.12) * mm, "radius": 6.63 * mm});
            skSolve(sketch);
        }
        {
            var Q0;
            Q0 = qSketchRegion(id + "F54", true);
            extrude(context, id + "F55", {"entities" : qUnion([Q0]), "operationType" : NewBodyOperationType.REMOVE, "oppositeDirection" : true, "depth" : 25 * mm, "offsetDistance" : 25 * mm});
        }
        {
            var Q0;
            Q0=makeQuery(id+"F52.opExtrude","CAP_FACE",FACE,{"disambiguationData":[OSD([sQuery(id+"F51.wireOp",EDGE,"E68"),sQuery(id+"F51.wireOp",EDGE,"E69")])],"isStart":false});
            var sketch = newSketch(context, id + "F56", { "sketchPlane" : qUnion([Q0])});
            skCircle(sketch, "E72", {"center": v(44.04, -0.12) * mm, "radius": 2.5 * mm});
            skCircle(sketch, "E73", {"center": v(44.04, -0.12) * mm, "radius": 3.88 * mm});
            skSolve(sketch);
        }
        {
            var Q0;
            Q0 = qSketchRegion(id + "F56", true);
            extrude(context, id + "F57", {"entities" : qUnion([Q0]), "operationType" : NewBodyOperationType.ADD, "depth" : 1.75 * mm, "offsetDistance" : 25 * mm});
        }
        {
            var Q0;
            Q0=makeQuery(id+"F57.opExtrude","CAP_EDGE",EDGE,{"disambiguationData":[OSD([sQuery(id+"F56.wireOp",EDGE,"E73")])],"isStart":false});
            fillet(context, id + "F58", {"entities" : qUnion([Q0]), "radius" : 0.75 * mm, "tangentPropagation" : true, "allowEdgeOverflow" : false});
        }
        {
            var Q0;
            Q0=qCreatedBy(makeId("Front.planeOp"),FACE);
            var sketch = newSketch(context, id + "F59", { "sketchPlane" : qUnion([Q0])});
            skCircle(sketch, "E74", {"center": v(-44.4, -10.54) * mm, "radius": 2.65 * mm});
            skCircle(sketch, "E75", {"center": v(-44.4, -10.54) * mm, "radius": 5 * mm});
            skSolve(sketch);
        }
        {
            var Q0;
            Q0 = qSketchRegion(id + "F59", true);
            extrude(context, id + "F60", {"entities" : qUnion([Q0]), "oppositeDirection" : true, "depth" : 1 * mm, "offsetDistance" : 25 * mm});
        }
        {
            var Q0;
            Q0=qCreatedBy(makeId("Top.planeOp"),FACE);
            var sketch = newSketch(context, id + "F61", { "sketchPlane" : qUnion([Q0])});
            skLineSegment(sketch, "E76", {"start": v(47.6, 27.95) * mm, "end": v(47.6, -4.13) * mm});
            skLineSegment(sketch, "E77", {"start": v(47.6, -4.13) * mm, "end": v(45.86, -4.13) * mm});
            skLineSegment(sketch, "E78", {"start": v(43.9, -2.45) * mm, "end": v(43.9, -2.05) * mm});
            skLineSegment(sketch, "E79", {"start": v(43.9, -2.05) * mm, "end": v(45.6, -2.05) * mm});
            skLineSegment(sketch, "E80", {"start": v(45.6, -2.05) * mm, "end": v(45.6, 27.54) * mm});
            skLineSegment(sketch, "E81", {"start": v(45.6, 27.54) * mm, "end": v(45.97, 27.95) * mm});
            skLineSegment(sketch, "E82", {"start": v(45.97, 27.95) * mm, "end": v(47.6, 27.95) * mm});
            skArc(sketch, "E83", {"start": v(45.86, -4.13) * mm, "mid": v(44.68, -3.53) * mm, "end": v(43.9, -2.45) * mm});
            skSolve(sketch);
        }
        {
            var Q0;
            Q0=makeQuery(id+"F61.imprint","IMPRINT",FACE,{"disambiguationData":[TD([[makeQuery(id+"F61.imprint","IMPRINT",EDGE,{"derivedFrom":sQuery(id+"F61.wireOp",EDGE,"E76")}),-1.0]])]});
            var Q1;
            Q1=sQuery(id+"F61.wireOp",EDGE,"E76");
            revolve(context, id + "F62", {"entities" : qUnion([Q0]), "axis" : qUnion([Q1]), "revolveType" : RevolveType.FULL});
        }
        {
            var Q0;
            Q0=makeQuery(id+"F62.opRevolve","SWEPT_FACE",FACE,{"disambiguationData":[OSD([sQuery(id+"F61.wireOp",EDGE,"E77")])]});
            var sketch = newSketch(context, id + "F63", { "sketchPlane" : qUnion([Q0])});
            skCircle(sketch, "E84.cCircle", {"center": v(47.6, 0) * mm, "radius": 1.25 * mm, "construction": true});
            skLineSegment(sketch, "E84.0", {"start": v(48.97, -0.48) * mm, "end": v(47.87, -1.42) * mm});
            skLineSegment(sketch, "E84.1", {"start": v(47.87, -1.42) * mm, "end": v(46.51, -0.94) * mm});
            skLineSegment(sketch, "E84.2", {"start": v(46.51, -0.94) * mm, "end": v(46.25, 0.48) * mm});
            skLineSegment(sketch, "E84.3", {"start": v(46.25, 0.48) * mm, "end": v(47.35, 1.42) * mm});
            skLineSegment(sketch, "E84.4", {"start": v(47.35, 1.42) * mm, "end": v(48.7, 0.94) * mm});
            skLineSegment(sketch, "E84.5", {"start": v(48.7, 0.94) * mm, "end": v(48.97, -0.48) * mm});
            skPoint(sketch, "E84.0.midPoint", {"position": v(48.42, -0.95) * mm});
            skSolve(sketch);
        }
        {
            var Q0;
            Q0 = qSketchRegion(id + "F63", true);
            extrude(context, id + "F64", {"entities" : qUnion([Q0]), "operationType" : NewBodyOperationType.REMOVE, "oppositeDirection" : true, "depth" : 1.3 * mm, "offsetDistance" : 25 * mm});
        }
        {
            var Q0;
            Q0=qCreatedBy(makeId("Front.planeOp"),FACE);
            var sketch = newSketch(context, id + "F65", { "sketchPlane" : qUnion([Q0])});
            skCircle(sketch, "E85", {"center": v(-28.82, -11.06) * mm, "radius": 2.15 * mm});
            skCircle(sketch, "E86", {"center": v(-28.82, -11.06) * mm, "radius": 4.5 * mm});
            skSolve(sketch);
        }
        {
            var Q0;
            Q0 = qSketchRegion(id + "F65", true);
            extrude(context, id + "F66", {"entities" : qUnion([Q0]), "depth" : 0.8 * mm, "offsetDistance" : 25 * mm});
        }
        {
            var Q0;
            Q0=qCreatedBy(makeId("Front.planeOp"),FACE);
            var sketch = newSketch(context, id + "F67", { "sketchPlane" : qUnion([Q0])});
            skCircle(sketch, "E87", {"center": v(-0.33, -11.42) * mm, "radius": 3.83 * mm});
            skCircle(sketch, "E88", {"center": v(-0.33, -11.42) * mm, "radius": 2 * mm});
            skSolve(sketch);
        }
        {
            var Q0;
            Q0 = qSketchRegion(id + "F67", true);
            extrude(context, id + "F68", {"entities" : qUnion([Q0]), "oppositeDirection" : true, "depth" : 3.25 * mm, "offsetDistance" : 25 * mm});
        }
        {
            var Q0;
            Q0=makeQuery(id+"F68.opExtrude","CAP_EDGE",EDGE,{"disambiguationData":[OSD([sQuery(id+"F67.wireOp",EDGE,"E87")])],"isStart":true});
            var Q1;
            Q1=makeQuery(id+"F68.opExtrude","CAP_EDGE",EDGE,{"disambiguationData":[OSD([sQuery(id+"F67.wireOp",EDGE,"E88")])],"isStart":true});
            var Q2;
            Q2=makeQuery(id+"F68.opExtrude","CAP_EDGE",EDGE,{"disambiguationData":[OSD([sQuery(id+"F67.wireOp",EDGE,"E87")])],"isStart":false});
            chamfer(context, id + "F69", {"entities" : qUnion([Q0, Q1, Q2]), "width" : 0.33 * mm, "tangentPropagation" : true});
        }
        {
            var Q0;
            Q0=makeQuery(id+"F68.opExtrude","CAP_FACE",FACE,{"disambiguationData":[OSD([sQuery(id+"F67.wireOp",EDGE,"E87"),sQuery(id+"F67.wireOp",EDGE,"E88")])],"isStart":false});
            var sketch = newSketch(context, id + "F70", { "sketchPlane" : qUnion([Q0])});
            skCircle(sketch, "E89", {"center": v(0.33, -11.42) * mm, "radius": 3.5 * mm});
            skSolve(sketch);
        }
        {
            var Q0;
            Q0 = qSketchRegion(id + "F70", true);
            extrude(context, id + "F71", {"entities" : qUnion([Q0]), "operationType" : NewBodyOperationType.ADD, "depth" : 4.75 * mm, "offsetDistance" : 25 * mm});
        }
        {
            var Q0;
            Q0=makeQuery(id+"F71.opExtrude","CAP_EDGE",EDGE,{"disambiguationData":[OSD([sQuery(id+"F70.wireOp",EDGE,"E89")])],"isStart":false});
            fillet(context, id + "F72", {"entities" : qUnion([Q0]), "radius" : 3.5 * mm, "tangentPropagation" : true, "allowEdgeOverflow" : false});
        }
        {
            var Q0;
            Q0=makeQuery(id+"F68.opExtrude","CAP_FACE",FACE,{"disambiguationData":[OSD([sQuery(id+"F67.wireOp",EDGE,"E87"),sQuery(id+"F67.wireOp",EDGE,"E88")])],"isStart":true});
            var sketch = newSketch(context, id + "F73", { "sketchPlane" : qUnion([Q0])});
            skCircle(sketch, "E90.cCircle", {"center": v(-0.33, -11.42) * mm, "radius": 3.5 * mm, "construction": true});
            skLineSegment(sketch, "E90.0", {"start": v(3.17, -9.4) * mm, "end": v(3.17, -13.44) * mm});
            skLineSegment(sketch, "E90.1", {"start": v(3.17, -13.44) * mm, "end": v(-0.33, -15.47) * mm});
            skLineSegment(sketch, "E90.2", {"start": v(-0.33, -15.47) * mm, "end": v(-3.83, -13.44) * mm});
            skLineSegment(sketch, "E90.3", {"start": v(-3.83, -13.44) * mm, "end": v(-3.83, -9.4) * mm});
            skLineSegment(sketch, "E90.4", {"start": v(-3.83, -9.4) * mm, "end": v(-0.33, -7.38) * mm});
            skLineSegment(sketch, "E90.5", {"start": v(-0.33, -7.38) * mm, "end": v(3.17, -9.4) * mm});
            skPoint(sketch, "E90.0.midPoint", {"position": v(3.17, -11.42) * mm});
            skCircle(sketch, "E91", {"center": v(-0.33, -11.42) * mm, "radius": 6.02 * mm});
            skSolve(sketch);
        }
        {
            var Q0;
            Q0 = qSketchRegion(id + "F73", true);
            extrude(context, id + "F74", {"entities" : qUnion([Q0]), "operationType" : NewBodyOperationType.REMOVE, "oppositeDirection" : true, "depth" : 25 * mm, "offsetDistance" : 25 * mm});
        }
    });
